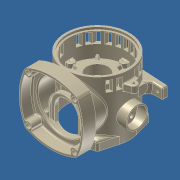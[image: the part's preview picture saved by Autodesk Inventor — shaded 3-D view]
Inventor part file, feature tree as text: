
AUTODESK INVENTOR PART (.ipt)
format: ipt  version: unknown  size: 2,481,152 bytes
history: native  units: in
note: dims shown in document units (in); Inventor stores cm internally (conversion verified against a paired STEP export)
features: extrude x28, sketch x24, plane x15, projected_geometry x10, loft x4, fillet x3, mirror x1, revolve x1, pattern_circular x1, chamfer x1
ambient origin geometry x8: Origin, YZ Plane, XZ Plane, XY Plane, X Axis, Y Axis, Z Axis, Center Point
bodies: Solid1 (feature_tree)
feature tree (88):
  extrude  "Extrusion1"  Depth=2.425in
  extrude  "Extrusion2"  Depth=0.1625in
  plane  "Work Plane3"
  sketch  "Sketch4"  dims[d7=3.375in d8=0.1in]
  plane  "Work Plane4"
  extrude  "Extrusion3"  Depth=0.1in
  sketch  "Sketch6"  dims[d11=0.1in d15=2.6693in]
  extrude  "Extrusion6"  Depth=0.1in
  extrude  "Extrusion7"  Depth=2.6693in
  sketch  "Sketch8"  dims[d19=2.625in d20=0.1in d21=0.0in]
  extrude  "Extrusion8"  Depth=0.575in TaperAngle=0.0deg
  extrude  "Extrusion10"  Depth=0.1in TaperAngle=0.0deg
  plane  "Work Plane5"
  sketch  "Sketch9"  dims[d24=3.15in d25=0.1in]
  extrude  "Extrusion12"  Depth=0.1in
  extrude  "Extrusion13"  Depth=0.1625in
  plane  "Work Plane6"
  extrude  "Extrusion15"  Depth=0.1in TaperAngle=0.0deg
  extrude  "Extrusion16"  Depth=0.5in TaperAngle=0.0deg
  plane  "Work Plane7"
  plane  "Work Plane8"
  plane  "Work Plane9"
  sketch  "Sketch15"  dims[d43=2.725in d44=0.0in d47=2.725in d48=0.0in]
  sketch  "Sketch13"  dims[d35=0.1in d38=0.5in d39=0.0in]
  extrude  "Extrusion19"  Depth=0.1in
  extrude  "Extrusion20"  Depth=2.725in TaperAngle=0.0deg
  plane  "Work Plane11"
  sketch  "Sketch14"  dims[d40=2.725in d41=0.0in d42=0.1in]
  extrude  "Extrusion21"  Depth=1.7in
  plane  "Work Plane12"
  extrude  "Extrusion22"  Depth=0.25in
  mirror  "Mirror3"
  extrude  "Extrusion23"  Depth=2.725in TaperAngle=0.0deg
  plane  "Work Plane15"
  sketch  "Sketch20"  dims[d55=0.0625in d58=2.725in d59=0.0in]
  plane  "Work Plane16"
  plane  "Work Plane17"
  extrude  "Extrusion30"  Depth=0.1in TaperAngle=0.0deg
  extrude  "Extrusion25"  Depth=0.75in
  extrude  "Extrusion26"  Depth=1.185in
  extrude  "Extrusion27"  Depth=0.25in TaperAngle=0.0deg
  extrude  "Extrusion29"  TaperAngle=0.0deg  [1 undecoded]
  extrude  "Extrusion31"  Depth=0.2375in
  extrude  "Extrusion32"  Depth=0.175in
  plane  "Work Plane18"
  extrude  "Extrusion33"  Depth=1.5748in
  plane  "Work Plane19"
  revolve  "Revolution1"  [1 undecoded]
  pattern_circular  "Circular Pattern1"  [2 undecoded]
  extrude  "Extrusion34"  Depth=0.7874in
  extrude  "Extrusion36"  Depth=0.675in
  sketch  "Sketch29"  dims[d83=0.25in d84=0.0in d85=0.2375in]
  plane  "Work Plane20"
  sketch  "Sketch30"  dims[d86=0.55in d87=0.175in]
  loft  "Loft1"
  loft  "Loft2"
  loft  "Loft3"
  loft  "Loft4"
  extrude  "Extrusion37"  Depth=0.4125in
  extrude  "Extrusion38"  Depth=1.0in
  fillet  "Fillet1"  Radius=1.1375in
  fillet  "Fillet3"  Radius=1.25in
  fillet  "Fillet4"  Radius=0.25in
  chamfer  "Chamfer1"  Distance=0.25in
  sketch  "Sketch1"  dims[d0=0.25in d1=2.425in]
  sketch  "Sketch2"  dims[d4=2.425in d5=0.1625in]
  projected_geometry  "Projected Loop1"
  projected_geometry  "Projected Loop2"
  sketch  "Sketch5"  dims[d9=0.1in d10=0.1in]
  sketch  "Sketch7"  dims[d16=2.6693in d17=0.575in d18=0.0in]
  projected_geometry  "Projected Loop3"
  projected_geometry  "Projected Loop4"
  sketch  "Sketch11"  dims[d27=0.25in d29=0.1625in]
  sketch  "Sketch12"  dims[d30=-0.05in d31=0.1in d32=0.0in]
  sketch  "Sketch16"  dims[d49=-0.125in d50=1.7in]
  sketch  "Sketch18"  dims[d51=0.25in d52=0.25in]
  projected_geometry  "Projected Loop6"
  sketch  "Sketch23"  dims[d60=0.175in d61=0.1in d62=0.0in]
  sketch  "Sketch24"  dims[d65=4.0in d66=0.75in]
  projected_geometry  "Projected Loop8"
  sketch  "Sketch25"  dims[d67=0.575in d69=1.185in]
  projected_geometry  "Projected Loop9"
  projected_geometry  "Projected Loop10"
  sketch  "Sketch26"  dims[d71=2.001in d72=0.25in d73=0.0in]
  sketch  "Sketch28"  dims[d81=0.375in d82=0.0in]
  projected_geometry  "Projected Loop12"
  sketch  "Sketch31"  dims[d95=1.5748in d97=0.3625in d98=0.3937in d100=1.0in d102=1.5748in d104=0.3625in d105=0.3937in d107=1.0in d111=0.2375in d112=0.7in d113=0.7874in d115=0.3625in d116=0.3937in d118=1.0in d120=0.675in d121=0.125in d122=0.2375in d123=0.2375in d124=3.05in d127=0.4125in d128=1.0in d129=1.1375in d130=1.25in d131=0.25in d132=0.0in d133=0.25in d134=0.0in d136=-0.5in d139=0.375in d140=0.125in d141=0.375in d142=0.0in d143=1.9175in d147=-0.125in d148=0.635in d149=0.5in d151=0.325in d152=0.375in d153=0.0in d154=0.375in d155=0.0in d156=1.1811in d158=360.0deg d160=0.175in d161=0.275in d167=-1.835in d168=0.1in d169=0.0in d170=1.125in d172=0.25in d173=0.175in d174=0.375in d175=0.175in d177=0.4125in d178=0.0in d179=45.0deg d180=0.175in d181=0.1875in d182=0.0875in d183=0.25in d184=0.0in d185=90.0deg d189=90.0deg d190=0.25in d191=0.175in d192=1.0in d193=0.0in d194=0.075in d195=1.265in d196=0.0in d197=1.265in d198=0.0in d199=1.265in d200=0.0in d201=90.0deg d202=0.175in d203=0.25in d204=1.265in d205=0.0in d206=90.0deg d208=0.175in d209=0.025in d210=90.0deg d211=1.5748in d212=360.0deg d214=0.0625in d216=0.375in d217=1.265in d218=0.0in d221=1.265in d222=0.0in d223=0.0312in d224=0.0312in d225=0.125in d226=0.125in d227=90.0deg d228=2.45in d229=-0.05in d230=0.225in d231=1.5748in d233=360.0deg d235=0.0in d236=90.0deg d237=0.0in d238=90.0deg d239=0.0in d240=90.0deg d241=0.0in d242=90.0deg d243=0.0in d244=90.0deg d245=0.0in d246=90.0deg d247=0.0in d248=90.0deg d249=0.0in d250=90.0deg d251=0.375in d252=0.0in d253=0.125in d254=0.0156in d255=0.125in d256=1.265in d257=0.0in d258=0.025in d259=0.125in d260=45.0deg]
  projected_geometry  "Projected Loop13"
note: 4 required parameter values undecoded (feature->parameter linkage not recoverable at this tier; creation-order binding heuristic only, values carry confidence <= 0.55)